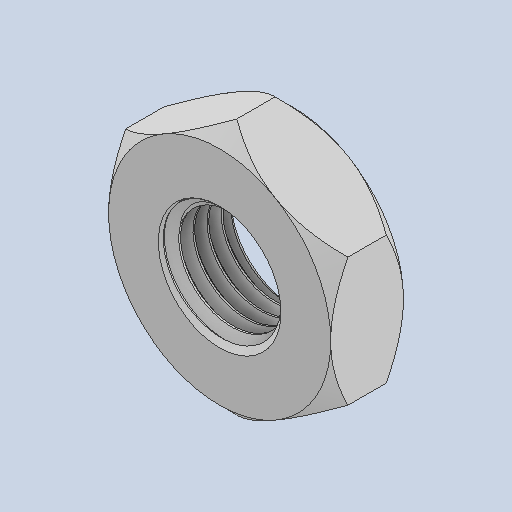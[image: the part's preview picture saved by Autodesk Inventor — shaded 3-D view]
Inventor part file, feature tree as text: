
AUTODESK INVENTOR PART (.ipt)
format: ipt  version: 2023 (Build 270158000, 158)  size: 274,944 bytes
history: native  units: mm
features: mirror x1
ambient origin geometry x8: Origin, YZ Plane, XZ Plane, XY Plane, X Axis, Y Axis, Z Axis, Center Point
bodies: Solid1 (feature_tree)
feature tree (1):
  mirror  "Mirror1"
